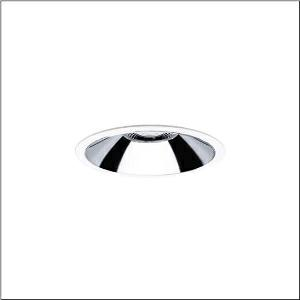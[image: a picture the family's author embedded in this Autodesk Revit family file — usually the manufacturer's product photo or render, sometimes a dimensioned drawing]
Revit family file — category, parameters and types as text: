
# Revit family: lunis_21_xl_51db15mf4d
name_source: partatom
category: Lighting Fixtures
units: mm (PartAtom-declared; Revit-internal decimal feet)

## family parameters
Cut with Voids When Loaded = No
Host = Face
Light Source = No
Part Type = Normal
Room Calculation Point = No
Round Connector Dimension = Use Diameter
Shared = No

## types (1)
- --- (1 x LED, 3000 lm, 24.3 W, 4000K)
    Apparent Load = 24 VA
    CIE Flux Codes = 89 99 100 100 100
    Color Rendering = 80
    Color Temperature = 4000K
    Default Elevation = 1800 mm
    Description = Lunis 21,  XL, downlight, of PC, light emission: direct distribution, LED rated luminous flux: 2.280lm, light colour: 840, control gear: ECG, with terminal, 3-pole, mains connection: 220..240V, AC, housing, round, of diecast aluminium, traffic white (RAL 9016), diameter: 213mm, protection rating (complete): IP20, protection rating (on room side): IP54, insulation class (complete): insulation class II (safety insulation), certification: CE, impact resistance: IK02, packaging unit: 1 piece
    Height = 0 mm  [stored 0 ft]
    Lamp = 1 x LED
    Lamp Light Flux = 3000 lm
    Lamp Power = 24.3 W
    Lamp count = 1
    Length = 213 mm
    Luminous efficacy = 123 lm/W
    Manufacturer = Siteco
    ModVariant = No
    Model = 51DB15MF4D
    Mounting Place = Ceiling
    Mounting Type = Recessed
    Number of Poles = 1
    OnlyDefault = Yes
    Power Factor = 1
    Product Name = Lunis 21 XL
    Product group = downlight
    ProductGroupID = 400
    Protection Class = Protection class II
    Protection Degree = IP 20
    RLX_Detail_Level = 1
    RLX_Emergency_Light_Flux = 0 lm
    RLX_Emergency_Type = 0
    RLX_Emergency_Type_DB = No
    RlxData = <blob elided: 27573 chars, md5=b93c1c74>
    Socket = socket
    Standby Power = 0 W
    System Light Flux = 3000 lm
    System Power = 24 W
    Type Comments = factory setting: luminous flux: 100 % | (ON | ON)
    Type Image = l_1287385.jpg
    URL = http://relux.com
    VarID = @adj_101045
    Voltage = 0 V
    Weight = 0.00 kg
    Width = 0 mm  [stored 0 ft]

note: [stored X ft] marks values corroborated as IEEE doubles in the binary element streams (Revit-internal decimal feet)

## geometry (parser evidence)
native form markers: Blend x4, Sweep x11
no freeform markers — native parametric forms only
